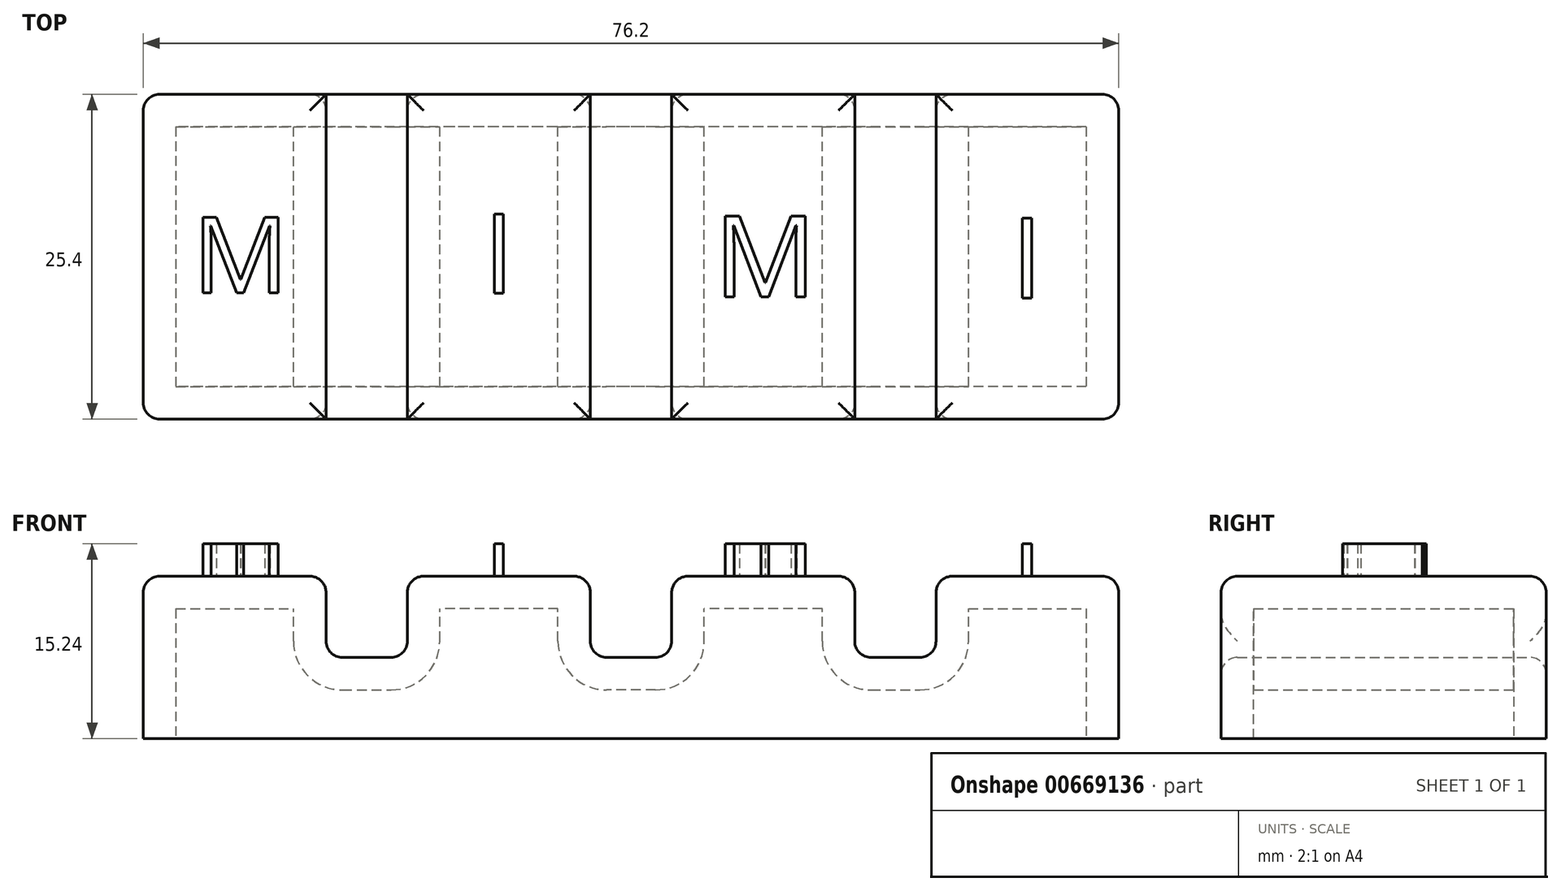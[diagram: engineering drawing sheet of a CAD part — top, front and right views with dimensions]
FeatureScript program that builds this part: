
annotation { "Feature Type Name" : "Feature", "Feature Type Description" : "" }
export const myFeature = defineFeature(function(context is Context, id is Id, definition is map)
    precondition{}
    {
        {
            var Q0;
            Q0=qCreatedBy(makeId("Top.planeOp"),FACE);
            var sketch = newSketch(context, id + "F0", { "sketchPlane" : qUnion([Q0])});
            skLineSegment(sketch, "E0.bottom", {"start": v(38.1, 12.7) * mm, "end": v(-38.1, 12.7) * mm});
            skLineSegment(sketch, "E0.top", {"start": v(38.1, -12.7) * mm, "end": v(-38.1, -12.7) * mm});
            skLineSegment(sketch, "E0.left", {"start": v(38.1, 12.7) * mm, "end": v(38.1, -12.7) * mm});
            skLineSegment(sketch, "E0.right", {"start": v(-38.1, 12.7) * mm, "end": v(-38.1, -12.7) * mm});
            skPoint(sketch, "E0.middle", {"position": v(0, 0) * mm});
            skSolve(sketch);
        }
        {
            var Q0;
            Q0 = qSketchRegion(id + "F0", true);
            extrude(context, id + "F1", {"entities" : qUnion([Q0]), "depth" : 12.7 * mm, "offsetDistance" : 25.4 * mm});
        }
        {
            var Q0;
            Q0=makeQuery(id+"F1.opExtrude","SWEPT_FACE",FACE,{"disambiguationData":[OSD([sQuery(id+"F0.wireOp",EDGE,"E0.bottom")])]});
            var sketch = newSketch(context, id + "F2", { "sketchPlane" : qUnion([Q0])});
            skLineSegment(sketch, "E1", {"start": v(-38.1, 6.35) * mm, "end": v(38.1, 6.35) * mm, "construction": true});
            skLineSegment(sketch, "E2.bottom", {"start": v(3.18, 6.35) * mm, "end": v(-3.17, 6.35) * mm});
            skLineSegment(sketch, "E2.top", {"start": v(3.18, 19.05) * mm, "end": v(-3.17, 19.05) * mm});
            skLineSegment(sketch, "E2.left", {"start": v(3.18, 6.35) * mm, "end": v(3.18, 19.05) * mm});
            skLineSegment(sketch, "E2.right", {"start": v(-3.17, 6.35) * mm, "end": v(-3.17, 19.05) * mm});
            skPoint(sketch, "E2.middle", {"position": v(0, 12.7) * mm});
            skLineSegment(sketch, "E3.bottom", {"start": v(-23.83, 6.35) * mm, "end": v(-17.48, 6.35) * mm});
            skLineSegment(sketch, "E3.top", {"start": v(-23.83, 19.05) * mm, "end": v(-17.48, 19.05) * mm});
            skLineSegment(sketch, "E3.left", {"start": v(-23.83, 6.35) * mm, "end": v(-23.83, 19.05) * mm});
            skLineSegment(sketch, "E3.right", {"start": v(-17.48, 6.35) * mm, "end": v(-17.48, 19.05) * mm});
            skPoint(sketch, "E3.middle", {"position": v(-20.65, 12.7) * mm});
            skLineSegment(sketch, "E4.bottom", {"start": v(17.48, 6.35) * mm, "end": v(23.83, 6.35) * mm});
            skLineSegment(sketch, "E4.top", {"start": v(17.48, 19.05) * mm, "end": v(23.83, 19.05) * mm});
            skLineSegment(sketch, "E4.left", {"start": v(17.48, 6.35) * mm, "end": v(17.48, 19.05) * mm});
            skLineSegment(sketch, "E4.right", {"start": v(23.83, 6.35) * mm, "end": v(23.83, 19.05) * mm});
            skPoint(sketch, "E4.middle", {"position": v(20.65, 12.7) * mm});
            skSolve(sketch);
        }
        {
            var Q0;
            Q0 = qSketchRegion(id + "F2", true);
            extrude(context, id + "F3", {"entities" : qUnion([Q0]), "operationType" : NewBodyOperationType.REMOVE, "endBound" : BoundingType.THROUGH_ALL, "oppositeDirection" : true, "depth" : 25.4 * mm, "offsetDistance" : 25.4 * mm});
        }
        {
            var Q0;
            {var subQ0=sQuery(id+"F0.wireOp",EDGE,"E0.bottom");var subQ1=sQuery(id+"F0.wireOp",EDGE,"E0.top");Q0=makeQuery(id+"F3.boolean.opBoolean","SPLIT",FACE,{"disambiguationData":[TD([makeQuery(id+"F3.opExtrude","SWEPT_FACE",FACE,{"disambiguationData":[OSD([sQuery(id+"F2.wireOp",EDGE,"E2.right")])]})])],"derivedFrom":makeQuery(id+"F1.opExtrude","CAP_FACE",FACE,{"disambiguationData":[OSD([subQ0,subQ1,sQuery(id+"F0.wireOp",EDGE,"E0.left"),sQuery(id+"F0.wireOp",EDGE,"E0.right")])],"isStart":false})});}
            var Q1;
            {var subQ0=sQuery(id+"F0.wireOp",EDGE,"E0.bottom");var subQ1=sQuery(id+"F0.wireOp",EDGE,"E0.top");var subQ2=sQuery(id+"F0.wireOp",EDGE,"E0.left");Q1=makeQuery(id+"F3.boolean.opBoolean","SPLIT",FACE,{"disambiguationData":[TD([makeQuery(id+"F1.opExtrude","SWEPT_FACE",FACE,{"disambiguationData":[OSD([subQ2])]})])],"derivedFrom":makeQuery(id+"F1.opExtrude","CAP_FACE",FACE,{"disambiguationData":[OSD([subQ0,subQ1,subQ2,sQuery(id+"F0.wireOp",EDGE,"E0.right")])],"isStart":false})});}
            var Q2;
            {var subQ0=sQuery(id+"F0.wireOp",EDGE,"E0.bottom");var subQ1=sQuery(id+"F0.wireOp",EDGE,"E0.top");Q2=makeQuery(id+"F3.boolean.opBoolean","SPLIT",FACE,{"disambiguationData":[TD([makeQuery(id+"F3.opExtrude","SWEPT_FACE",FACE,{"disambiguationData":[OSD([sQuery(id+"F2.wireOp",EDGE,"E2.left")])]})])],"derivedFrom":makeQuery(id+"F1.opExtrude","CAP_FACE",FACE,{"disambiguationData":[OSD([subQ0,subQ1,sQuery(id+"F0.wireOp",EDGE,"E0.left"),sQuery(id+"F0.wireOp",EDGE,"E0.right")])],"isStart":false})});}
            var Q3;
            {var subQ0=sQuery(id+"F0.wireOp",EDGE,"E0.bottom");var subQ1=sQuery(id+"F0.wireOp",EDGE,"E0.right");var subQ2=sQuery(id+"F0.wireOp",EDGE,"E0.top");Q3=makeQuery(id+"F3.boolean.opBoolean","SPLIT",FACE,{"disambiguationData":[TD([makeQuery(id+"F1.opExtrude","SWEPT_FACE",FACE,{"disambiguationData":[OSD([subQ1])]})])],"derivedFrom":makeQuery(id+"F1.opExtrude","CAP_FACE",FACE,{"disambiguationData":[OSD([subQ0,subQ2,sQuery(id+"F0.wireOp",EDGE,"E0.left"),subQ1])],"isStart":false})});}
            var Q4;
            Q4=makeQuery(id+"F3.boolean.opBoolean","COPY",FACE,{"derivedFrom":makeQuery(id+"F3.opExtrude","SWEPT_FACE",FACE,{"disambiguationData":[OSD([sQuery(id+"F2.wireOp",EDGE,"E3.bottom")])]})});
            var Q5;
            Q5=makeQuery(id+"F3.boolean.opBoolean","COPY",FACE,{"derivedFrom":makeQuery(id+"F3.opExtrude","SWEPT_FACE",FACE,{"disambiguationData":[OSD([sQuery(id+"F2.wireOp",EDGE,"E2.bottom")])]})});
            var Q6;
            Q6=makeQuery(id+"F3.boolean.opBoolean","COPY",FACE,{"derivedFrom":makeQuery(id+"F3.opExtrude","SWEPT_FACE",FACE,{"disambiguationData":[OSD([sQuery(id+"F2.wireOp",EDGE,"E4.bottom")])]})});
            var Q7;
            Q7=makeQuery(id+"F1.opExtrude","SWEPT_EDGE",EDGE,{"disambiguationData":[OSD([sQuery(id+"F0.wireOp",EDGE,"E0.bottom"),sQuery(id+"F0.wireOp",EDGE,"E0.right")])]});
            var Q8;
            Q8=makeQuery(id+"F1.opExtrude","SWEPT_EDGE",EDGE,{"disambiguationData":[OSD([sQuery(id+"F0.wireOp",EDGE,"E0.bottom"),sQuery(id+"F0.wireOp",EDGE,"E0.left")])]});
            var Q9;
            Q9=makeQuery(id+"F1.opExtrude","SWEPT_EDGE",EDGE,{"disambiguationData":[OSD([sQuery(id+"F0.wireOp",EDGE,"E0.top"),sQuery(id+"F0.wireOp",EDGE,"E0.left")])]});
            var Q10;
            Q10=makeQuery(id+"F1.opExtrude","SWEPT_EDGE",EDGE,{"disambiguationData":[OSD([sQuery(id+"F0.wireOp",EDGE,"E0.top"),sQuery(id+"F0.wireOp",EDGE,"E0.right")])]});
            fillet(context, id + "F4", {"entities" : qUnion([Q0, Q1, Q2, Q3, Q4, Q5, Q6, Q7, Q8, Q9, Q10]), "radius" : 1.27 * mm, "tangentPropagation" : true, "allowEdgeOverflow" : false});
        }
        {
            var Q0;
            Q0=makeQuery(id+"F1.opExtrude","CAP_FACE",FACE,{"disambiguationData":[OSD([sQuery(id+"F0.wireOp",EDGE,"E0.bottom"),sQuery(id+"F0.wireOp",EDGE,"E0.top"),sQuery(id+"F0.wireOp",EDGE,"E0.left"),sQuery(id+"F0.wireOp",EDGE,"E0.right")])],"isStart":true});
            shell(context, id + "F5", {"entities" : qUnion([Q0]), "thickness" : 2.54 * mm});
        }
        {
            var Q0;
            {var subQ0=sQuery(id+"F0.wireOp",EDGE,"E0.bottom");var subQ1=sQuery(id+"F0.wireOp",EDGE,"E0.top");Q0=makeQuery(id+"F3.boolean.opBoolean","SPLIT",FACE,{"disambiguationData":[TD([makeQuery(id+"F3.opExtrude","SWEPT_FACE",FACE,{"disambiguationData":[OSD([sQuery(id+"F2.wireOp",EDGE,"E2.right")])]})])],"derivedFrom":makeQuery(id+"F1.opExtrude","CAP_FACE",FACE,{"disambiguationData":[OSD([subQ0,subQ1,sQuery(id+"F0.wireOp",EDGE,"E0.left"),sQuery(id+"F0.wireOp",EDGE,"E0.right")])],"isStart":false})});}
            var sketch = newSketch(context, id + "F6", { "sketchPlane" : qUnion([Q0])});
            skText(sketch, "E5", { "text": "M", "fontName": "OpenSans-Regular.ttf"});
            skText(sketch, "E6", { "text": "M", "fontName": "OpenSans-Regular.ttf"});
            skText(sketch, "E7", { "text": "I", "fontName": "OpenSans-Regular.ttf"});
            skText(sketch, "E8", { "text": "I", "fontName": "OpenSans-Regular.ttf"});
            const initialGuessF6  = {"E5": [0.0065, -0.00313, 1, 0, 0.00635], "E6": [-0.03425, -0.00283, 1, 0, 0.00597], "E7": [-0.01154, -0.00286, 1, 0, 0.00625], "E8": [0.02972, -0.00323, 1, 0, 0.00629]};
            skSetInitialGuess(sketch, initialGuessF6);
            skSolve(sketch);
        }
        {
            var Q0;
            Q0 = qSketchRegion(id + "F6", true);
            extrude(context, id + "F7", {"entities" : qUnion([Q0]), "operationType" : NewBodyOperationType.ADD, "depth" : 2.54 * mm, "offsetDistance" : 25.4 * mm});
        }
    });
